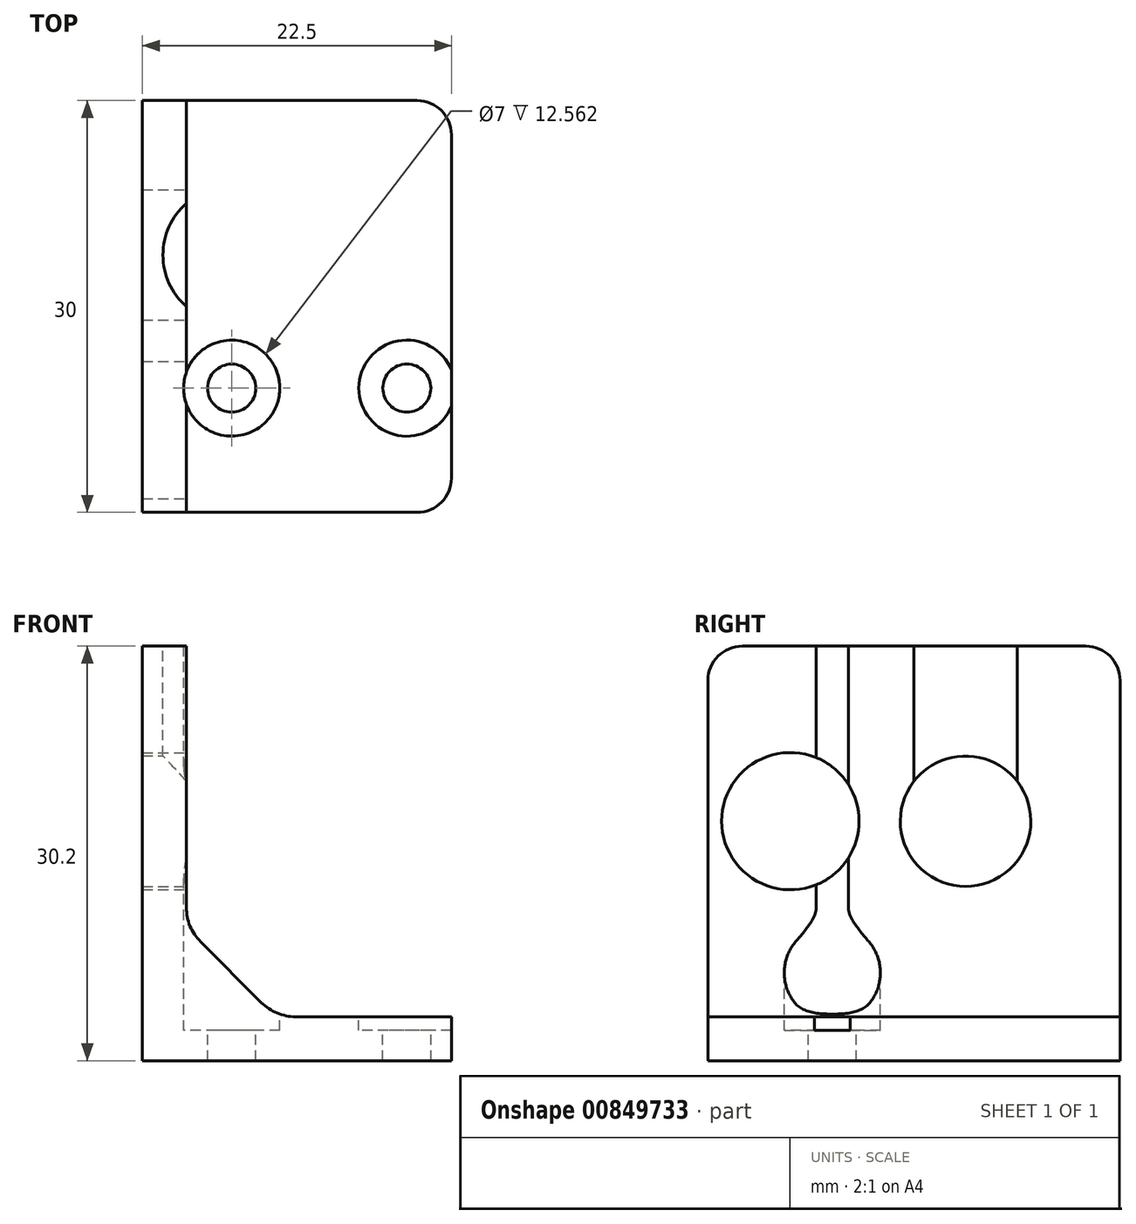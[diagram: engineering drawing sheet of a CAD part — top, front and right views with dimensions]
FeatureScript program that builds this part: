
annotation { "Feature Type Name" : "Feature", "Feature Type Description" : "" }
export const myFeature = defineFeature(function(context is Context, id is Id, definition is map)
    precondition{}
    {
        {
            var Q0;
            Q0=qCreatedBy(makeId("Front.planeOp"),FACE);
            var sketch = newSketch(context, id + "F0", { "sketchPlane" : qUnion([Q0])});
            skLineSegment(sketch, "E0", {"start": v(0, 0) * mm, "end": v(22.5, 0) * mm});
            skLineSegment(sketch, "E1", {"start": v(0, 0) * mm, "end": v(0, 30.2) * mm});
            skLineSegment(sketch, "E2", {"start": v(0, 30.2) * mm, "end": v(3.2, 30.2) * mm});
            skLineSegment(sketch, "E3", {"start": v(22.5, 0) * mm, "end": v(22.5, 3.2) * mm});
            skLineSegment(sketch, "E4", {"start": v(3.2, 30.2) * mm, "end": v(3.2, 3.2) * mm});
            skLineSegment(sketch, "E5", {"start": v(22.5, 3.2) * mm, "end": v(3.2, 3.2) * mm});
            skSolve(sketch);
        }
        {
            var Q0;
            Q0 = qSketchRegion(id + "F0", true);
            extrude(context, id + "F1", {"entities" : qUnion([Q0]), "depth" : 30 * mm, "offsetDistance" : 25 * mm});
        }
        {
            var Q0;
            Q0=makeQuery(id+"F1.opExtrude","SWEPT_FACE",FACE,{"disambiguationData":[OSD([sQuery(id+"F0.wireOp",EDGE,"E5")])]});
            var sketch = newSketch(context, id + "F2", { "sketchPlane" : qUnion([Q0])});
            skPoint(sketch, "E6", {"position": v(19.25, -20.95) * mm});
            skPoint(sketch, "E7", {"position": v(6.5, -20.95) * mm});
            skSolve(sketch);
        }
        {
            var Q0;
            Q0=sQuery(id+"F2.wireOp",VERTEX,"E6");
            var Q1;
            Q1=sQuery(id+"F2.wireOp",VERTEX,"E7");
            var Q2;
            Q2=makeQuery(id+"F1.opExtrude","SWEPT_BODY",BODY,{"disambiguationData":[OSD([sQuery(id+"F0.wireOp",EDGE,"E0"),sQuery(id+"F0.wireOp",EDGE,"E1"),sQuery(id+"F0.wireOp",EDGE,"E2"),sQuery(id+"F0.wireOp",EDGE,"E3"),sQuery(id+"F0.wireOp",EDGE,"E4"),sQuery(id+"F0.wireOp",EDGE,"E5")])]});
            hole(context, id + "F3", {"style" : HoleStyle.C_BORE, "endStyle" : HoleEndStyle.THROUGH, "holeDiameter" : 3.5 * mm, "cBoreDiameter" : 7 * mm, "cBoreDepth" : 1 * mm, "majorDiameter" : 5 * mm, "isTappedThrough" : true, "tappedDepth" : 12 * mm, "tapClearance" : 3, "locations" : qUnion([Q0, Q1]), "scope" : qUnion([Q2])});
        }
        {
            var Q0;
            Q0=makeQuery(id+"F1.opExtrude","SWEPT_FACE",FACE,{"disambiguationData":[OSD([sQuery(id+"F0.wireOp",EDGE,"E4")])]});
            var sketch = newSketch(context, id + "F4", { "sketchPlane" : qUnion([Q0])});
            skPoint(sketch, "E8", {"position": v(-11.25, 17.45) * mm});
            skPoint(sketch, "E9", {"position": v(-24, 17.45) * mm});
            skSolve(sketch);
        }
        {
            var Q0;
            Q0=sQuery(id+"F4.wireOp",VERTEX,"E8");
            var Q1;
            Q1=makeQuery(id+"F1.opExtrude","SWEPT_BODY",BODY,{"disambiguationData":[OSD([sQuery(id+"F0.wireOp",EDGE,"E0"),sQuery(id+"F0.wireOp",EDGE,"E1"),sQuery(id+"F0.wireOp",EDGE,"E2"),sQuery(id+"F0.wireOp",EDGE,"E3"),sQuery(id+"F0.wireOp",EDGE,"E4"),sQuery(id+"F0.wireOp",EDGE,"E5")])]});
            hole(context, id + "F5", {"style" : HoleStyle.SIMPLE, "endStyle" : HoleEndStyle.BLIND, "holeDiameter" : 9.5 * mm, "majorDiameter" : 5 * mm, "holeDepth" : 5 * mm, "isTappedThrough" : true, "tappedDepth" : 12 * mm, "tapClearance" : 3, "locations" : qUnion([Q0]), "scope" : qUnion([Q1])});
        }
        {
            var Q0;
            Q0=sQuery(id+"F2.wireOp",VERTEX,"E7");
            var Q1;
            Q1=makeQuery(id+"F1.opExtrude","SWEPT_BODY",BODY,{"disambiguationData":[OSD([sQuery(id+"F0.wireOp",EDGE,"E0"),sQuery(id+"F0.wireOp",EDGE,"E1"),sQuery(id+"F0.wireOp",EDGE,"E2"),sQuery(id+"F0.wireOp",EDGE,"E3"),sQuery(id+"F0.wireOp",EDGE,"E4"),sQuery(id+"F0.wireOp",EDGE,"E5")])]});
            hole(context, id + "F6", {"style" : HoleStyle.SIMPLE, "endStyle" : HoleEndStyle.THROUGH, "oppositeDirection" : true, "holeDiameter" : 7 * mm, "majorDiameter" : 5 * mm, "isTappedThrough" : true, "tappedDepth" : 12 * mm, "tapClearance" : 3, "locations" : qUnion([Q0]), "scope" : qUnion([Q1])});
        }
        {
            var Q0;
            Q0=makeQuery(id+"F1.opExtrude","SWEPT_FACE",FACE,{"disambiguationData":[OSD([sQuery(id+"F0.wireOp",EDGE,"E2")])]});
            var sketch = newSketch(context, id + "F7", { "sketchPlane" : qUnion([Q0])});
            skPoint(sketch, "E10", {"position": v(6.5, -11.25) * mm});
            skSolve(sketch);
        }
        {
            var Q0;
            Q0=sQuery(id+"F7.wireOp",VERTEX,"E10");
            var Q1;
            Q1=makeQuery(id+"F1.opExtrude","SWEPT_BODY",BODY,{"disambiguationData":[OSD([sQuery(id+"F0.wireOp",EDGE,"E0"),sQuery(id+"F0.wireOp",EDGE,"E1"),sQuery(id+"F0.wireOp",EDGE,"E2"),sQuery(id+"F0.wireOp",EDGE,"E3"),sQuery(id+"F0.wireOp",EDGE,"E4"),sQuery(id+"F0.wireOp",EDGE,"E5")])]});
            hole(context, id + "F8", {"style" : HoleStyle.SIMPLE, "endStyle" : HoleEndStyle.BLIND, "holeDiameter" : 10 * mm, "majorDiameter" : 5 * mm, "holeDepth" : 10 * mm, "isTappedThrough" : true, "tappedDepth" : 12 * mm, "tapClearance" : 3, "locations" : qUnion([Q0]), "scope" : qUnion([Q1])});
        }
        {
            var Q0;
            Q0=makeQuery(id+"F1.opExtrude","CAP_EDGE",EDGE,{"disambiguationData":[OSD([sQuery(id+"F0.wireOp",EDGE,"E3")])],"isStart":true});
            var Q1;
            Q1=makeQuery(id+"F1.opExtrude","CAP_EDGE",EDGE,{"disambiguationData":[OSD([sQuery(id+"F0.wireOp",EDGE,"E3")])],"isStart":false});
            var Q2;
            Q2=makeQuery(id+"F1.opExtrude","CAP_EDGE",EDGE,{"disambiguationData":[OSD([sQuery(id+"F0.wireOp",EDGE,"E2")])],"isStart":false});
            var Q3;
            Q3=makeQuery(id+"F1.opExtrude","CAP_EDGE",EDGE,{"disambiguationData":[OSD([sQuery(id+"F0.wireOp",EDGE,"E2")])],"isStart":true});
            fillet(context, id + "F9", {"entities" : qUnion([Q0, Q1, Q2, Q3]), "radius" : 2.5 * mm, "tangentPropagation" : true, "allowEdgeOverflow" : false});
        }
        {
            var Q0;
            {var subQ0=sQuery(id+"F0.wireOp",EDGE,"E5");var subQ1=makeQuery(id+"F1.opExtrude","SWEPT_FACE",FACE,{"disambiguationData":[OSD([subQ0])]});var subQ2=sQuery(id+"F0.wireOp",EDGE,"E4");var subQ3=makeQuery(id+"F1.opExtrude","SWEPT_FACE",FACE,{"disambiguationData":[OSD([subQ2])]});Q0=makeQuery(id+"F3.hole-1.boolean.opBoolean","SPLIT",EDGE,{"disambiguationData":[topologyDisambiguationEdgeConnected([subQ3,subQ1]),TD([makeQuery(id+"F1.opExtrude","CAP_FACE",FACE,{"disambiguationData":[OSD([sQuery(id+"F0.wireOp",EDGE,"E0"),sQuery(id+"F0.wireOp",EDGE,"E1"),sQuery(id+"F0.wireOp",EDGE,"E2"),sQuery(id+"F0.wireOp",EDGE,"E3"),subQ2,subQ0])],"isStart":true})])],"derivedFrom":makeQuery(id+"F1.opExtrude","SWEPT_EDGE",EDGE,{"disambiguationData":[OSD([subQ2,subQ0])]})});}
            var Q1;
            {var subQ0=sQuery(id+"F0.wireOp",EDGE,"E4");var subQ1=makeQuery(id+"F1.opExtrude","SWEPT_FACE",FACE,{"disambiguationData":[OSD([subQ0])]});var subQ2=sQuery(id+"F0.wireOp",EDGE,"E5");var subQ3=makeQuery(id+"F1.opExtrude","SWEPT_FACE",FACE,{"disambiguationData":[OSD([subQ2])]});Q1=makeQuery(id+"F3.hole-1.boolean.opBoolean","SPLIT",EDGE,{"disambiguationData":[topologyDisambiguationEdgeConnected([subQ1,subQ3]),TD([makeQuery(id+"F1.opExtrude","CAP_FACE",FACE,{"disambiguationData":[OSD([sQuery(id+"F0.wireOp",EDGE,"E0"),sQuery(id+"F0.wireOp",EDGE,"E1"),sQuery(id+"F0.wireOp",EDGE,"E2"),sQuery(id+"F0.wireOp",EDGE,"E3"),subQ0,subQ2])],"isStart":false})])],"derivedFrom":makeQuery(id+"F1.opExtrude","SWEPT_EDGE",EDGE,{"disambiguationData":[OSD([subQ0,subQ2])]})});}
            chamfer(context, id + "F10", {"entities" : qUnion([Q0, Q1]), "width" : 6.5 * mm, "tangentPropagation" : true});
        }
        {
            var Q0;
            {var subQ0=sQuery(id+"F0.wireOp",EDGE,"E5");var subQ1=makeQuery(id+"F1.opExtrude","SWEPT_FACE",FACE,{"disambiguationData":[OSD([subQ0])]});var subQ2=sQuery(id+"F0.wireOp",EDGE,"E4");var subQ3=makeQuery(id+"F1.opExtrude","SWEPT_FACE",FACE,{"disambiguationData":[OSD([subQ2])]});Q0=makeQuery(id+"F10.opChamfer","BLEND_EDGE",EDGE,{"blendedFrom":[makeQuery(id+"F3.hole-1.boolean.opBoolean","SPLIT",EDGE,{"disambiguationData":[topologyDisambiguationEdgeConnected([subQ3,subQ1]),TD([makeQuery(id+"F1.opExtrude","CAP_FACE",FACE,{"disambiguationData":[OSD([sQuery(id+"F0.wireOp",EDGE,"E0"),sQuery(id+"F0.wireOp",EDGE,"E1"),sQuery(id+"F0.wireOp",EDGE,"E2"),sQuery(id+"F0.wireOp",EDGE,"E3"),subQ2,subQ0])],"isStart":true})])],"derivedFrom":makeQuery(id+"F1.opExtrude","SWEPT_EDGE",EDGE,{"disambiguationData":[OSD([subQ2,subQ0])]})}),subQ1],"blendedInto":[subQ1]});}
            var Q1;
            {var subQ1=sQuery(id+"F0.wireOp",EDGE,"E5");var subQ2=sQuery(id+"F0.wireOp",EDGE,"E4");var subQ3=sQuery(id+"F0.wireOp",EDGE,"E2");var subQ4=makeQuery(id+"F1.opExtrude","CAP_FACE",FACE,{"disambiguationData":[OSD([sQuery(id+"F0.wireOp",EDGE,"E0"),sQuery(id+"F0.wireOp",EDGE,"E1"),subQ3,sQuery(id+"F0.wireOp",EDGE,"E3"),subQ2,subQ1])],"isStart":true});var subQ5=makeQuery(id+"F1.opExtrude","SWEPT_FACE",FACE,{"disambiguationData":[OSD([subQ1])]});var subQ6=makeQuery(id+"F1.opExtrude","SWEPT_FACE",FACE,{"disambiguationData":[OSD([subQ2])]});Q1=makeQuery(id+"F10.opChamfer","BLEND_EDGE",EDGE,{"blendedFrom":[makeQuery(id+"F3.hole-1.boolean.opBoolean","SPLIT",EDGE,{"disambiguationData":[topologyDisambiguationEdgeConnected([subQ6,subQ5]),TD([subQ4])],"derivedFrom":makeQuery(id+"F1.opExtrude","SWEPT_EDGE",EDGE,{"disambiguationData":[OSD([subQ2,subQ1])]})}),makeQuery(id+"F6.hole-0.boolean.opBoolean","SPLIT",FACE,{"disambiguationData":[TD([makeQuery(id+"F5.hole-0.boolean.opBoolean","COPY",FACE,{"derivedFrom":makeQuery(id+"F5.hole-0.opRevolve","SWEPT_FACE",FACE,{"disambiguationData":[OSD([sQuery(id+"F5.hole-0.sketch.wireOp",EDGE,"core_line_2")])]})})])],"derivedFrom":subQ6})],"blendedInto":[makeQuery(id+"F6.hole-0.boolean.opBoolean","SPLIT",FACE,{"disambiguationData":[TD([makeQuery(id+"F5.hole-0.boolean.opBoolean","COPY",FACE,{"derivedFrom":makeQuery(id+"F5.hole-0.opRevolve","SWEPT_FACE",FACE,{"disambiguationData":[OSD([sQuery(id+"F5.hole-0.sketch.wireOp",EDGE,"core_line_2")])]})})])],"derivedFrom":subQ6})]});}
            var Q2;
            {var subQ0=sQuery(id+"F0.wireOp",EDGE,"E2");var subQ2=sQuery(id+"F0.wireOp",EDGE,"E5");var subQ3=makeQuery(id+"F1.opExtrude","SWEPT_FACE",FACE,{"disambiguationData":[OSD([subQ2])]});var subQ4=sQuery(id+"F0.wireOp",EDGE,"E4");var subQ5=makeQuery(id+"F1.opExtrude","CAP_FACE",FACE,{"disambiguationData":[OSD([sQuery(id+"F0.wireOp",EDGE,"E0"),sQuery(id+"F0.wireOp",EDGE,"E1"),subQ0,sQuery(id+"F0.wireOp",EDGE,"E3"),subQ4,subQ2])],"isStart":false});var subQ6=makeQuery(id+"F1.opExtrude","SWEPT_FACE",FACE,{"disambiguationData":[OSD([subQ4])]});Q2=makeQuery(id+"F10.opChamfer","BLEND_EDGE",EDGE,{"blendedFrom":[makeQuery(id+"F3.hole-1.boolean.opBoolean","SPLIT",EDGE,{"disambiguationData":[topologyDisambiguationEdgeConnected([subQ6,subQ3]),TD([subQ5])],"derivedFrom":makeQuery(id+"F1.opExtrude","SWEPT_EDGE",EDGE,{"disambiguationData":[OSD([subQ4,subQ2])]})}),makeQuery(id+"F6.hole-0.boolean.opBoolean","SPLIT",FACE,{"disambiguationData":[TD([subQ5])],"derivedFrom":subQ6})],"blendedInto":[makeQuery(id+"F6.hole-0.boolean.opBoolean","SPLIT",FACE,{"disambiguationData":[TD([subQ5])],"derivedFrom":subQ6})]});}
            fillet(context, id + "F11", {"entities" : qUnion([Q0, Q1, Q2]), "radius" : 3.5 * mm, "tangentPropagation" : true, "allowEdgeOverflow" : false});
        }
        {
            var Q0;
            Q0=sQuery(id+"F4.wireOp",VERTEX,"E9");
            var Q1;
            Q1=makeQuery(id+"F1.opExtrude","SWEPT_BODY",BODY,{"disambiguationData":[OSD([sQuery(id+"F0.wireOp",EDGE,"E0"),sQuery(id+"F0.wireOp",EDGE,"E1"),sQuery(id+"F0.wireOp",EDGE,"E2"),sQuery(id+"F0.wireOp",EDGE,"E3"),sQuery(id+"F0.wireOp",EDGE,"E4"),sQuery(id+"F0.wireOp",EDGE,"E5")])]});
            hole(context, id + "F12", {"style" : HoleStyle.SIMPLE, "endStyle" : HoleEndStyle.THROUGH, "holeDiameter" : 10 * mm, "majorDiameter" : 5 * mm, "isTappedThrough" : true, "tappedDepth" : 12 * mm, "tapClearance" : 3, "locations" : qUnion([Q0]), "scope" : qUnion([Q1])});
        }
    });
